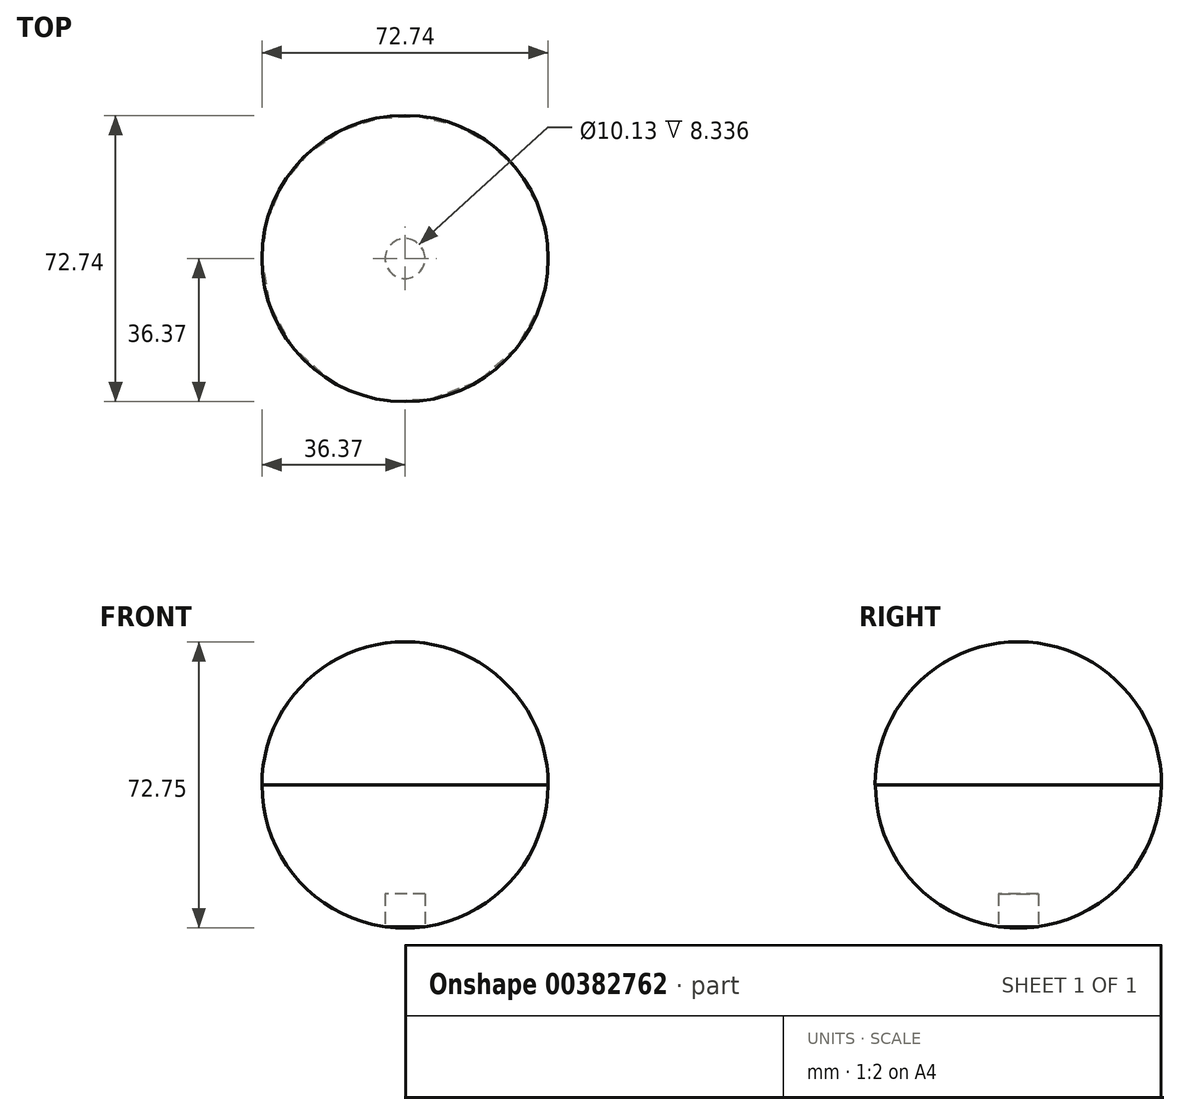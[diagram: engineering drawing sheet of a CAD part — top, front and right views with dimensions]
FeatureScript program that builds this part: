
annotation { "Feature Type Name" : "Feature", "Feature Type Description" : "" }
export const myFeature = defineFeature(function(context is Context, id is Id, definition is map)
    precondition{}
    {
        {
            var Q0;
            Q0=qCreatedBy(makeId("Top.planeOp"),FACE);
            var sketch = newSketch(context, id + "F0", { "sketchPlane" : qUnion([Q0])});
            skCircle(sketch, "E0", {"center": v(0, 0) * mm, "radius": 36.37 * mm});
            skSolve(sketch);
        }
        {
            var Q0;
            Q0=qSketchRegion(id+"F0",true);
            extrude(context, id + "F1", {"entities" : qUnion([Q0]), "depth" : 72.75 * mm});
        }
        {
            var Q0;
            Q0=makeQuery(id+"F1.opExtrude","CAP_EDGE",EDGE,{"disambiguationData":[OSD([sQuery(id+"F0.wireOp",EDGE,"E0")])],"isStart":false});
            fillet(context, id + "F2", {"entities" : qUnion([Q0]), "radius" : 36.35 * mm, "tangentPropagation" : true, "allowEdgeOverflow" : false});
        }
        {
            var Q0;
            Q0=makeQuery(id+"F1.opExtrude","CAP_FACE",FACE,{"disambiguationData":[OSD([sQuery(id+"F0.wireOp",EDGE,"E0")])],"isStart":true});
            var Q1;
            {var subQ0=sQuery(id+"F0.wireOp",EDGE,"E0");Q1=makeQuery(id+"F2.opFillet","BLEND_EDGE",EDGE,{"blendedFrom":[makeQuery(id+"F1.opExtrude","CAP_EDGE",EDGE,{"disambiguationData":[OSD([subQ0])],"isStart":false}),makeQuery(id+"F1.opExtrude","SWEPT_FACE",FACE,{"disambiguationData":[OSD([subQ0])]})],"blendedInto":[makeQuery(id+"F1.opExtrude","SWEPT_FACE",FACE,{"disambiguationData":[OSD([subQ0])]})]});}
            fillet(context, id + "F3", {"entities" : qUnion([Q0, Q1]), "radius" : 36.35 * mm, "tangentPropagation" : true, "allowEdgeOverflow" : false});
        }
        {
            var Q0;
            Q0=qCreatedBy(makeId("Top.planeOp"),FACE);
            var sketch = newSketch(context, id + "F4", { "sketchPlane" : qUnion([Q0])});
            skCircle(sketch, "E1", {"center": v(0, 0) * mm, "radius": 5.07 * mm});
            skSolve(sketch);
        }
        {
            var Q0;
            Q0=qSketchRegion(id+"F4",true);
            extrude(context, id + "F5", {"entities" : qUnion([Q0]), "operationType" : NewBodyOperationType.REMOVE, "depth" : 8.7 * mm});
        }
    });
